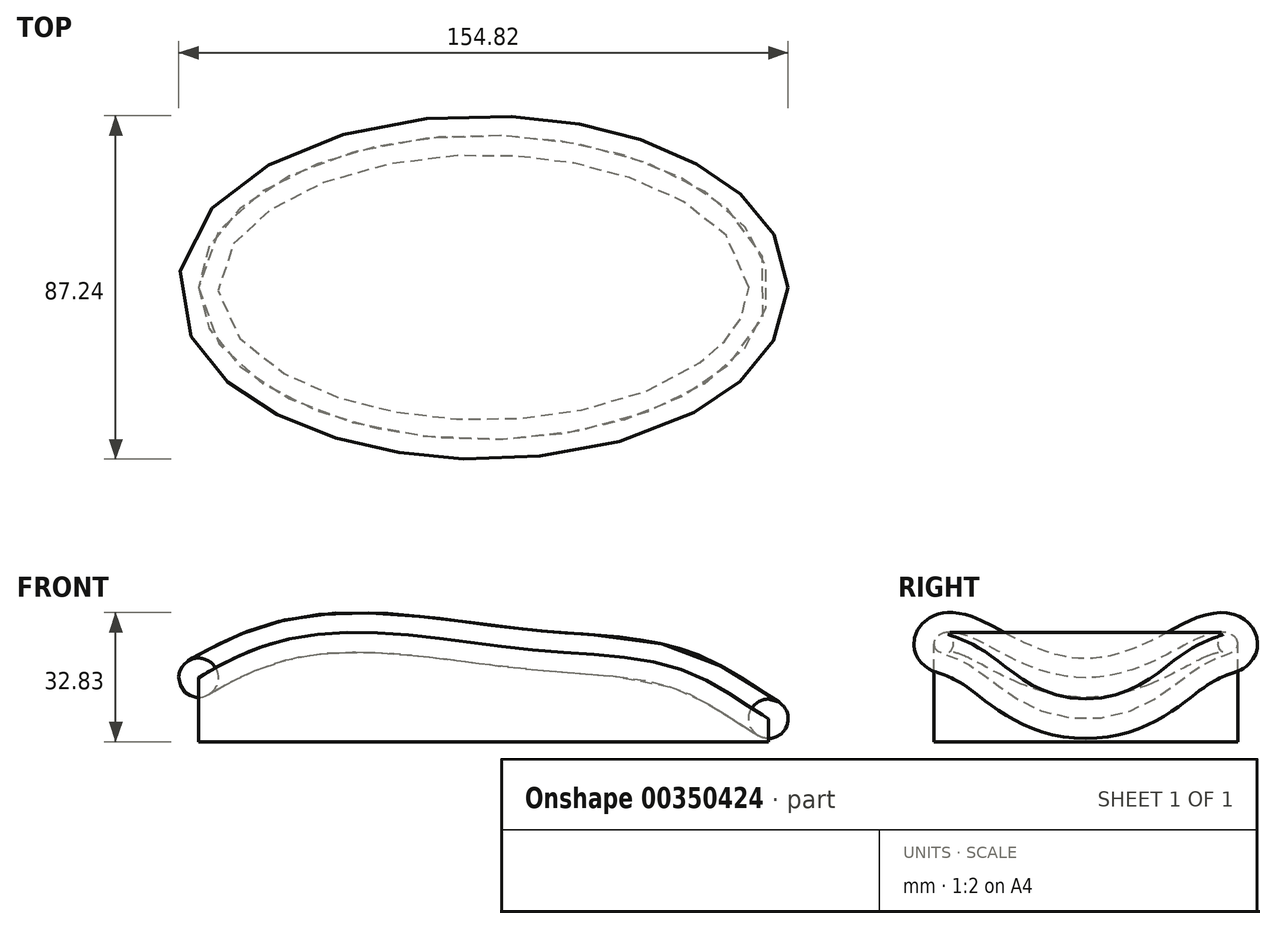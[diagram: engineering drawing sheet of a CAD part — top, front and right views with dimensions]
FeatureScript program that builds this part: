
annotation { "Feature Type Name" : "Feature", "Feature Type Description" : "" }
export const myFeature = defineFeature(function(context is Context, id is Id, definition is map)
    precondition{}
    {
        {
            var Q0;
            Q0=qCreatedBy(makeId("Top.planeOp"),FACE);
            var sketch = newSketch(context, id + "F0", { "sketchPlane" : qUnion([Q0])});
            skEllipse(sketch, "E0", {"center": v(0, 0) * mm, "majorRadius": 72.4 * mm, "minorRadius": 38.62 * mm, "majorAxis": v(-1, 0)});
            skSolve(sketch);
        }
        {
            var Q0;
            Q0=makeQuery(id+"F0.imprint","IMPRINT",FACE,{"disambiguationData":[TD([[makeQuery(id+"F0.imprint","IMPRINT",EDGE,{"derivedFrom":sQuery(id+"F0.wireOp",EDGE,"E0")}),1.0]])]});
            extrude(context, id + "F1", {"entities" : qUnion([Q0]), "depth" : 50 * mm});
        }
        {
            var Q0;
            Q0=qCreatedBy(makeId("Front.planeOp"),FACE);
            var sketch = newSketch(context, id + "F2", { "sketchPlane" : qUnion([Q0])});
            skFitSpline(sketch, "E1", {"points": [v(119.32, 0) * mm, v(84.14, 0) * mm, v(52.74, 17.4) * mm, v(11.48, 23.45) * mm, v(-47.97, 26.43) * mm, v(-95, 0) * mm], "startDerivative": vector(-206.22, -30.6) * mm, "endDerivative": vector(-200.25, -155.9) * mm});
            skLineSegment(sketch, "E2", {"start": v(-95, 0) * mm, "end": v(-95, 116.15) * mm});
            skLineSegment(sketch, "E3", {"start": v(-95, 116.15) * mm, "end": v(136.93, 116.15) * mm});
            skLineSegment(sketch, "E4", {"start": v(136.93, 116.15) * mm, "end": v(119.32, 0) * mm});
            skSolve(sketch);
        }
        {
            var Q0;
            Q0=makeQuery(id+"F2.imprint","IMPRINT",FACE,{"disambiguationData":[TD([[makeQuery(id+"F2.imprint","IMPRINT",EDGE,{"derivedFrom":sQuery(id+"F2.wireOp",EDGE,"E1")}),-1.0]])]});
            extrude(context, id + "F3", {"entities" : qUnion([Q0]), "operationType" : NewBodyOperationType.REMOVE, "oppositeDirection" : true, "depth" : 100 * mm, "hasSecondDirection" : true, "secondDirectionOppositeDirection" : false, "secondDirectionDepth" : 50 * mm});
        }
        {
            var Q0;
            Q0=qCreatedBy(makeId("Front.planeOp"),FACE);
            var sketch = newSketch(context, id + "F4", { "sketchPlane" : qUnion([Q0])});
            skCircle(sketch, "E5", {"center": v(72.4, 5.85) * mm, "radius": 5 * mm});
            skPoint(sketch, "E6.orphan", {"position": v(-72.4, 16.28) * mm});
            skSolve(sketch);
        }
        {
            var Q0;
            Q0=makeQuery(id+"F4.imprint","IMPRINT",FACE,{"disambiguationData":[TD([[makeQuery(id+"F4.imprint","IMPRINT",EDGE,{"derivedFrom":sQuery(id+"F4.wireOp",EDGE,"E5")}),1.0]])]});
            var Q1;
            Q1=makeQuery(id+"F3.boolean.opBoolean","INTERSECT",EDGE,{"derivedFrom":[makeQuery(id+"F1.opExtrude","SWEPT_FACE",FACE,{"disambiguationData":[OSD([sQuery(id+"F0.wireOp",EDGE,"E0")])]}),makeQuery(id+"F3.opExtrude","SWEPT_FACE",FACE,{"disambiguationData":[OSD([sQuery(id+"F2.wireOp",EDGE,"E1")])]})]});
            sweep(context, id + "F5", {"profiles" : qUnion([Q0]), "path" : qUnion([Q1])});
        }
    });
